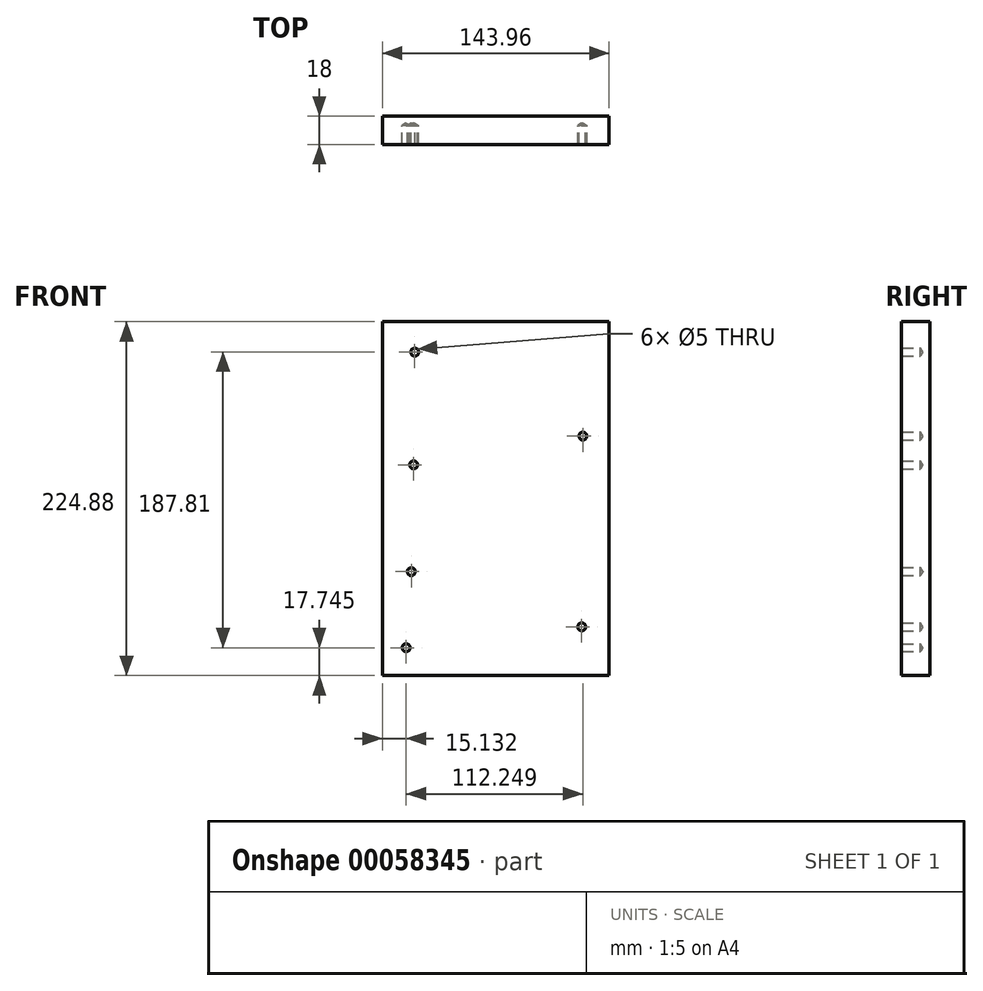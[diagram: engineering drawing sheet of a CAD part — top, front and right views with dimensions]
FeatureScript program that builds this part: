
annotation { "Feature Type Name" : "Feature", "Feature Type Description" : "" }
export const myFeature = defineFeature(function(context is Context, id is Id, definition is map)
    precondition{}
    {
        {
            var Q0;
            Q0=qCreatedBy(makeId("Front.planeOp"),FACE);
            var sketch = newSketch(context, id + "F0", { "sketchPlane" : qUnion([Q0])});
            skLineSegment(sketch, "E0.rect.bottom", {"start": v(71.98, 112.44) * mm, "end": v(-71.98, 112.44) * mm});
            skLineSegment(sketch, "E0.rect.top", {"start": v(71.98, -112.44) * mm, "end": v(-71.98, -112.44) * mm});
            skLineSegment(sketch, "E0.rect.left", {"start": v(71.98, 112.44) * mm, "end": v(71.98, -112.44) * mm});
            skLineSegment(sketch, "E0.rect.right", {"start": v(-71.98, 112.44) * mm, "end": v(-71.98, -112.44) * mm});
            skPoint(sketch, "E0.rect.middle", {"position": v(0, 0) * mm});
            skSolve(sketch);
        }
        {
            var Q0;
            Q0 = qSketchRegion(id + "F0", true);
            extrude(context, id + "F1", {"entities" : qUnion([Q0]), "depth" : 18 * mm});
        }
        {
            var Q0;
            Q0=makeQuery(id+"F1.opExtrude","CAP_FACE",FACE,{"disambiguationData":[OSD([sQuery(id+"F0.wireOp",EDGE,"E0.rect.bottom"),sQuery(id+"F0.wireOp",EDGE,"E0.rect.top"),sQuery(id+"F0.wireOp",EDGE,"E0.rect.left"),sQuery(id+"F0.wireOp",EDGE,"E0.rect.right")])],"isStart":false});
            var sketch = newSketch(context, id + "F2", { "sketchPlane" : qUnion([Q0])});
            skPoint(sketch, "E1", {"position": v(-51.38, 93.11) * mm});
            skPoint(sketch, "E2", {"position": v(-52.11, 21.47) * mm});
            skPoint(sketch, "E3", {"position": v(-53.57, -46.37) * mm});
            skPoint(sketch, "E4", {"position": v(-56.85, -94.7) * mm});
            skPoint(sketch, "E5", {"position": v(54.67, -81.45) * mm});
            skPoint(sketch, "E6", {"position": v(55.4, 39.75) * mm});
            skSolve(sketch);
        }
        {
            var Q0;
            Q0=sQuery(id+"F2.wireOp",VERTEX,"E6");
            var Q1;
            Q1=sQuery(id+"F2.wireOp",VERTEX,"E2");
            var Q2;
            Q2=sQuery(id+"F2.wireOp",VERTEX,"E1");
            var Q3;
            Q3=sQuery(id+"F2.wireOp",VERTEX,"E3");
            var Q4;
            Q4=sQuery(id+"F2.wireOp",VERTEX,"E4");
            var Q5;
            Q5=sQuery(id+"F2.wireOp",VERTEX,"E5");
            var Q6;
            Q6=makeQuery(id+"F1.opExtrude","SWEPT_BODY",BODY,{"disambiguationData":[OSD([sQuery(id+"F0.wireOp",EDGE,"E0.rect.bottom"),sQuery(id+"F0.wireOp",EDGE,"E0.rect.top"),sQuery(id+"F0.wireOp",EDGE,"E0.rect.left"),sQuery(id+"F0.wireOp",EDGE,"E0.rect.right")])]});
            hole(context, id + "F3", {"style" : HoleStyle.SIMPLE, "holeDiameter" : 5 * mm, "endStyle" : HoleEndStyle.BLIND, "holeDepth" : 12 * mm, "locations" : qUnion([Q0, Q1, Q2, Q3, Q4, Q5]), "scope" : qUnion([Q6])});
        }
    });
